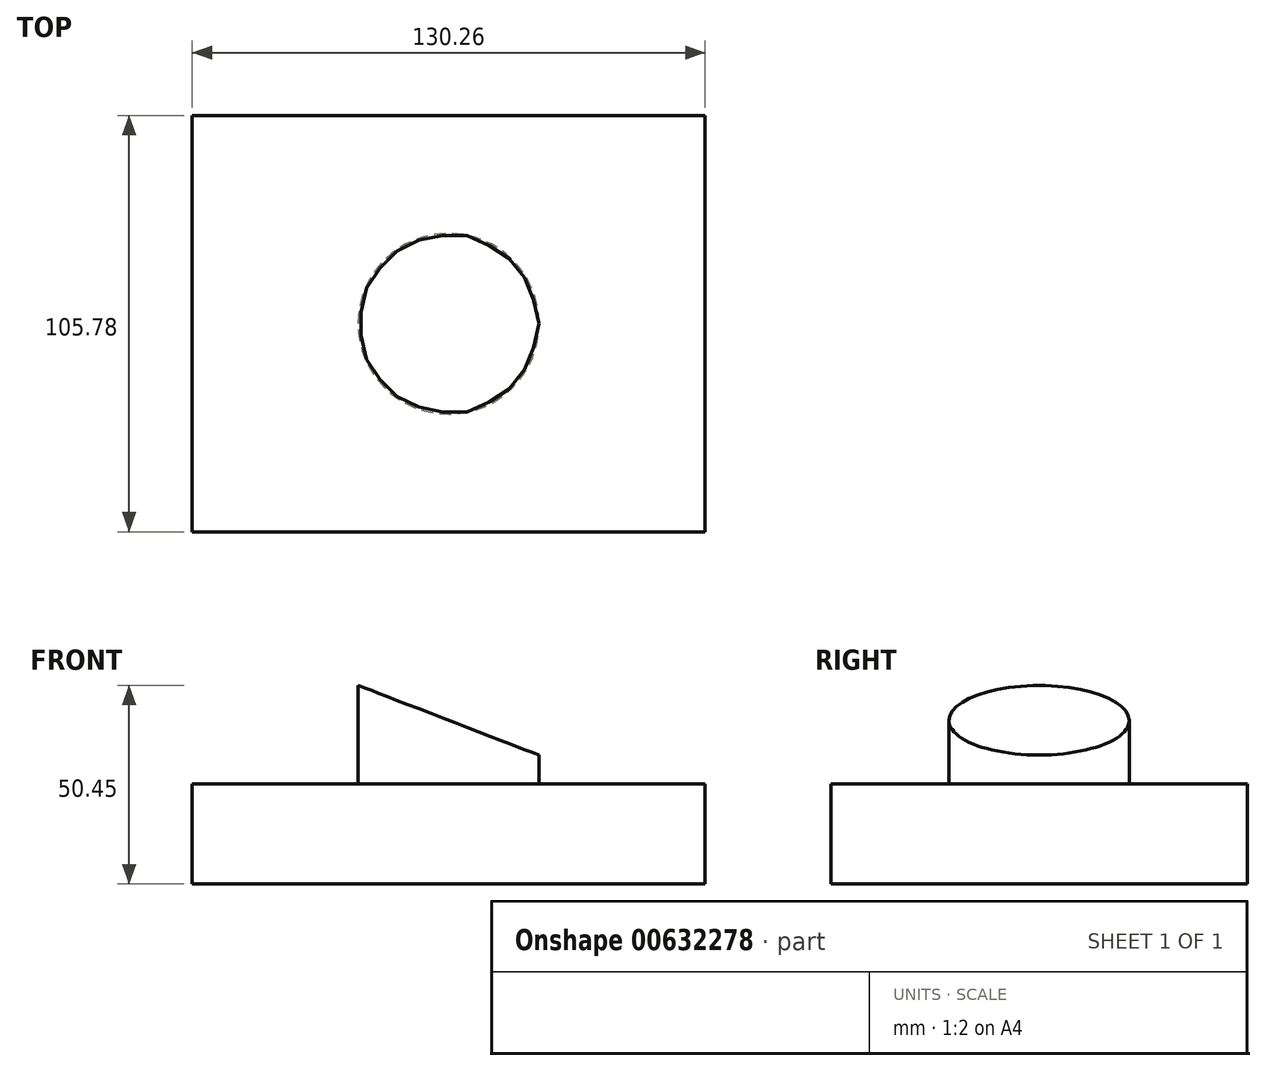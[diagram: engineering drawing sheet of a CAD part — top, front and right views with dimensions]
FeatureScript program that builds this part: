
annotation { "Feature Type Name" : "Feature", "Feature Type Description" : "" }
export const myFeature = defineFeature(function(context is Context, id is Id, definition is map)
    precondition{}
    {
        {
            var Q0;
            Q0=qCreatedBy(makeId("Top.planeOp"),FACE);
            var sketch = newSketch(context, id + "F0", { "sketchPlane" : qUnion([Q0])});
            skCircle(sketch, "E0", {"center": v(0, 0) * mm, "radius": 22.95 * mm});
            skSolve(sketch);
        }
        {
            var Q0;
            Q0=makeQuery(id+"F0.imprint","IMPRINT",FACE,{"disambiguationData":[TD([[makeQuery(id+"F0.imprint","IMPRINT",EDGE,{"derivedFrom":sQuery(id+"F0.wireOp",EDGE,"E0")}),1.0]])]});
            extrude(context, id + "F1", {"entities" : qUnion([Q0]), "depth" : 50.8 * mm, "offsetDistance" : 25.4 * mm});
        }
        {
            var Q0;
            Q0=qCreatedBy(makeId("Top.planeOp"),FACE);
            var sketch = newSketch(context, id + "F2", { "sketchPlane" : qUnion([Q0])});
            skLineSegment(sketch, "E1.bottom", {"start": v(-65.13, 52.89) * mm, "end": v(65.13, 52.89) * mm});
            skLineSegment(sketch, "E1.top", {"start": v(-65.13, -52.89) * mm, "end": v(65.13, -52.89) * mm});
            skLineSegment(sketch, "E1.left", {"start": v(-65.13, 52.89) * mm, "end": v(-65.13, -52.89) * mm});
            skLineSegment(sketch, "E1.right", {"start": v(65.13, 52.89) * mm, "end": v(65.13, -52.89) * mm});
            skPoint(sketch, "E1.middle", {"position": v(0, 0) * mm});
            skSolve(sketch);
        }
        {
            var Q0;
            Q0=makeQuery(id+"F2.imprint","IMPRINT",FACE,{"disambiguationData":[TD([[makeQuery(id+"F2.imprint","IMPRINT",EDGE,{"derivedFrom":sQuery(id+"F2.wireOp",EDGE,"E1.bottom")}),-1.0]])]});
            extrude(context, id + "F3", {"entities" : qUnion([Q0]), "operationType" : NewBodyOperationType.ADD, "depth" : 25.4 * mm, "offsetDistance" : 25.4 * mm});
        }
        {
            var Q0;
            Q0=qCreatedBy(makeId("Front.planeOp"),FACE);
            var sketch = newSketch(context, id + "F4", { "sketchPlane" : qUnion([Q0])});
            skLineSegment(sketch, "E2", {"start": v(-29.97, 53.16) * mm, "end": v(31.8, 53.16) * mm});
            skLineSegment(sketch, "E3", {"start": v(-29.97, 53.16) * mm, "end": v(31.8, 29.33) * mm});
            skLineSegment(sketch, "E4", {"start": v(31.8, 29.33) * mm, "end": v(33.45, 53.16) * mm});
            skLineSegment(sketch, "E5", {"start": v(33.3, 50.98) * mm, "end": v(33.45, 53.16) * mm});
            skLineSegment(sketch, "E6", {"start": v(31.8, 53.16) * mm, "end": v(33.45, 53.16) * mm});
            skSolve(sketch);
        }
        {
            var Q0;
            Q0=makeQuery(id+"F4.imprint","IMPRINT",FACE,{"disambiguationData":[TD([[makeQuery(id+"F4.imprint","IMPRINT",EDGE,{"derivedFrom":sQuery(id+"F4.wireOp",EDGE,"E2")}),-1.0]])]});
            extrude(context, id + "F5", {"entities" : qUnion([Q0]), "operationType" : NewBodyOperationType.REMOVE, "endBound" : BoundingType.SYMMETRIC, "depth" : 254 * mm, "offsetDistance" : 25.4 * mm});
        }
    });
